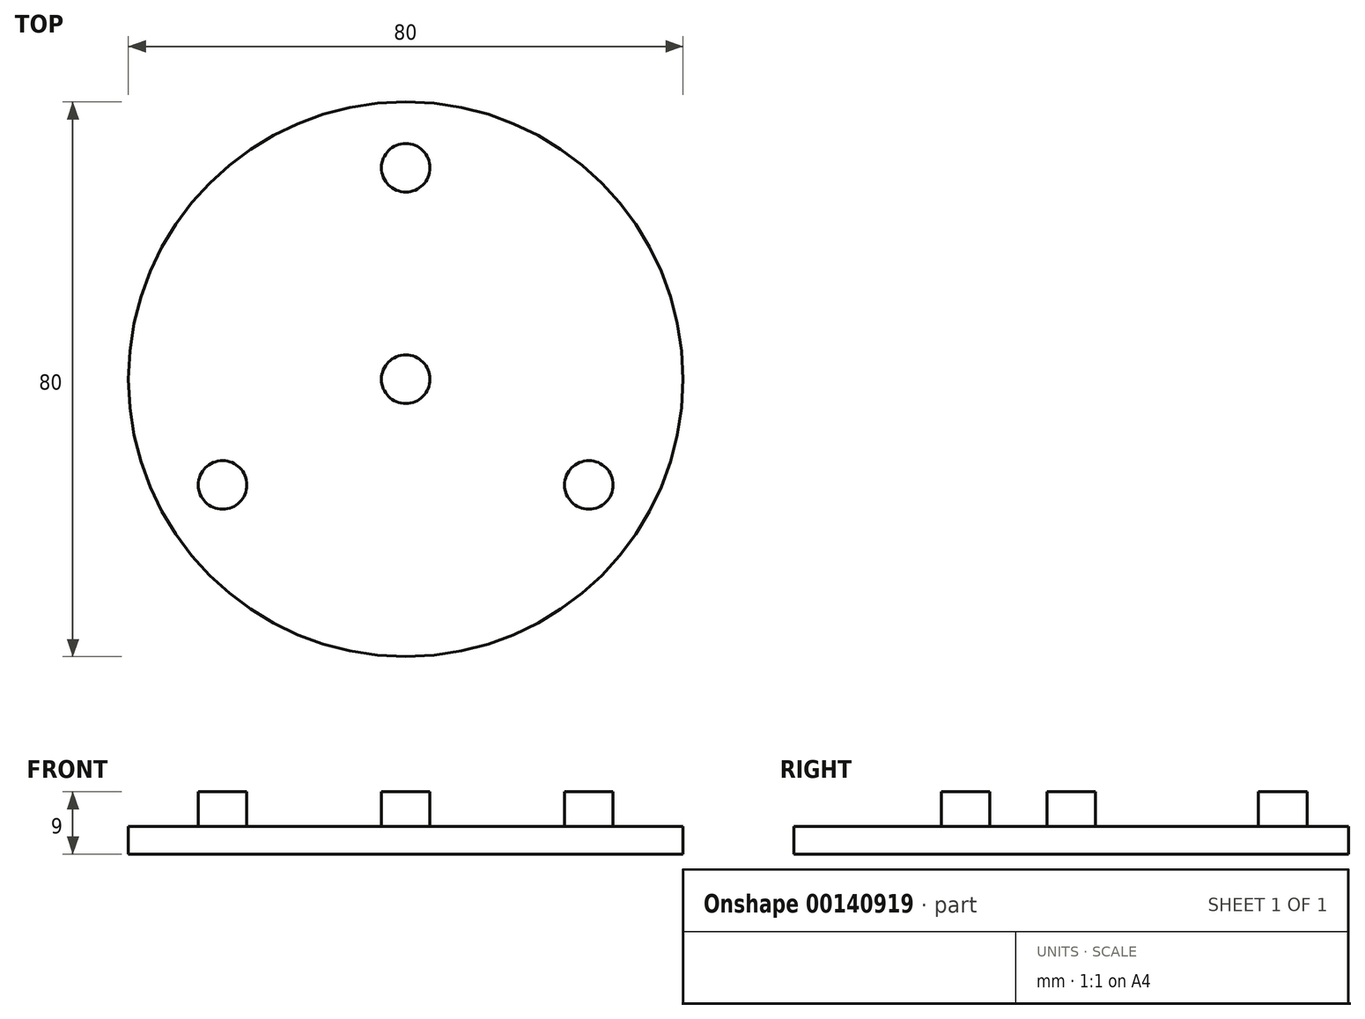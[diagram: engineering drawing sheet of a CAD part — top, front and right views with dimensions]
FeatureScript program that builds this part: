
annotation { "Feature Type Name" : "Feature", "Feature Type Description" : "" }
export const myFeature = defineFeature(function(context is Context, id is Id, definition is map)
    precondition{}
    {
        {
            var Q0;
            Q0=qCreatedBy(makeId("Top.planeOp"),FACE);
            var sketch = newSketch(context, id + "F0", { "sketchPlane" : qUnion([Q0])});
            skCircle(sketch, "E0", {"center": v(0, 0) * mm, "radius": 40 * mm});
            skSolve(sketch);
        }
        {
            var Q0;
            Q0 = qSketchRegion(id + "F0", true);
            extrude(context, id + "F1", {"entities" : qUnion([Q0]), "oppositeDirection" : true, "depth" : 4 * mm});
        }
        {
            var Q0;
            Q0=makeQuery(id+"F1.opExtrude","CAP_FACE",FACE,{"disambiguationData":[OSD([sQuery(id+"F0.wireOp",EDGE,"E0")])],"isStart":true});
            var sketch = newSketch(context, id + "F2", { "sketchPlane" : qUnion([Q0])});
            skCircle(sketch, "E1", {"center": v(0, 0) * mm, "radius": 3.5 * mm});
            skCircle(sketch, "E2", {"center": v(0, 0) * mm, "radius": 30.5 * mm, "construction": true});
            skCircle(sketch, "E3", {"center": v(0, 30.5) * mm, "radius": 3.5 * mm});
            skCircle(sketch, "E4.1.0", {"center": v(-26.41, -15.25) * mm, "radius": 3.5 * mm});
            skCircle(sketch, "E4.2.0", {"center": v(26.41, -15.25) * mm, "radius": 3.5 * mm});
            skSolve(sketch);
        }
        {
            var Q0;
            Q0 = qSketchRegion(id + "F2", true);
            extrude(context, id + "F3", {"entities" : qUnion([Q0]), "operationType" : NewBodyOperationType.ADD, "depth" : 5 * mm});
        }
    });
